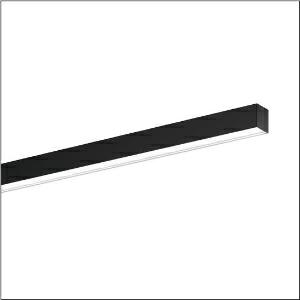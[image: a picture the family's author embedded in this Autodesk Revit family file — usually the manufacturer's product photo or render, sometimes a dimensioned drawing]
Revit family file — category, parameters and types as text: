
# Revit family: silica_r__21_51mx20tat2b_5805
name_source: partatom
category: Lighting Fixtures
units: mm (PartAtom-declared; Revit-internal decimal feet)

## family parameters
Cut with Voids When Loaded = No
Host = Face
Light Source = No
Part Type = Normal
Room Calculation Point = No
Round Connector Dimension = Use Diameter
Shared = No

## types (1)
- --- (1 x LED, 2400 lm, 20.5 W, 6500K)
    Apparent Load = 21 VA
    CIE Flux Codes = 48 79 96 100 100
    Color Rendering = 80
    Color Temperature = 6500K
    Default Elevation = 1800 mm
    Description = Silica® 21, office luminaire, primary optical cover: cover, of PMMA, opal, light emission: direct distribution, primary light characteristic: symmetric, installation type: surface-mounted, LED, rated luminous flux: 2.400lm, luminous efficacy: 112lm/W, light colour: 8tw, colour temperature: 2700..6500K, control gear: ECG DALI, with terminal, 3+2-pole, max. 2.5mm², mains connection: 220..240V, AC, 50/60Hz, rated input power: 21.5W, luminaire housing, of aluminium, jet black (RAL 9005), length: 1.204mm, width: 53mm, height: 53mm, protection rating (complete): IP20, insulation class (complete): insulation class I (protective earthing), certification: CE, permissible operating ambient temperature: 0..+35°C, standard: EN 50419, packaging unit: 1 piece
    Height = 0 mm  [stored 0 ft]
    Lamp = 1 x LED
    Lamp Light Flux = 2400 lm
    Lamp Power = 20.5 W
    Lamp count = 1
    Length = 1204 mm
    Luminous efficacy = 117 lm/W
    Manufacturer = Siteco
    ModVariant = No
    Model = 51MX20TAT2B
    Mounting Place = Ceiling
    Mounting Type = Recessed
    Number of Poles = 1
    OnlyDefault = Yes
    Power Factor = 1
    Product Name = Silica® 21
    Product group = office luminaire | ceiling recessed
    ProductGroupID = 400
    Protection Class = Protection class I
    Protection Degree = IP 20
    RLX_Detail_Level = 1
    RLX_Emergency_Light_Flux = 0 lm
    RLX_Emergency_Type = 0
    RLX_Emergency_Type_DB = No
    RlxData = <blob elided: 25689 chars, md5=de9d60a7>
    Socket = socket
    Standby Power = 0 W
    System Light Flux = 2400 lm
    System Power = 21 W
    Type Comments = individual setting
    Type Image = l_1335925.jpg
    URL = http://relux.com
    VarID = @adj_109495
    Voltage = 0 V
    Weight = 0.00 kg
    Width = 53 mm

note: [stored X ft] marks values corroborated as IEEE doubles in the binary element streams (Revit-internal decimal feet)

## geometry (parser evidence)
native form markers: Blend x4, Sweep x9
no freeform markers — native parametric forms only
